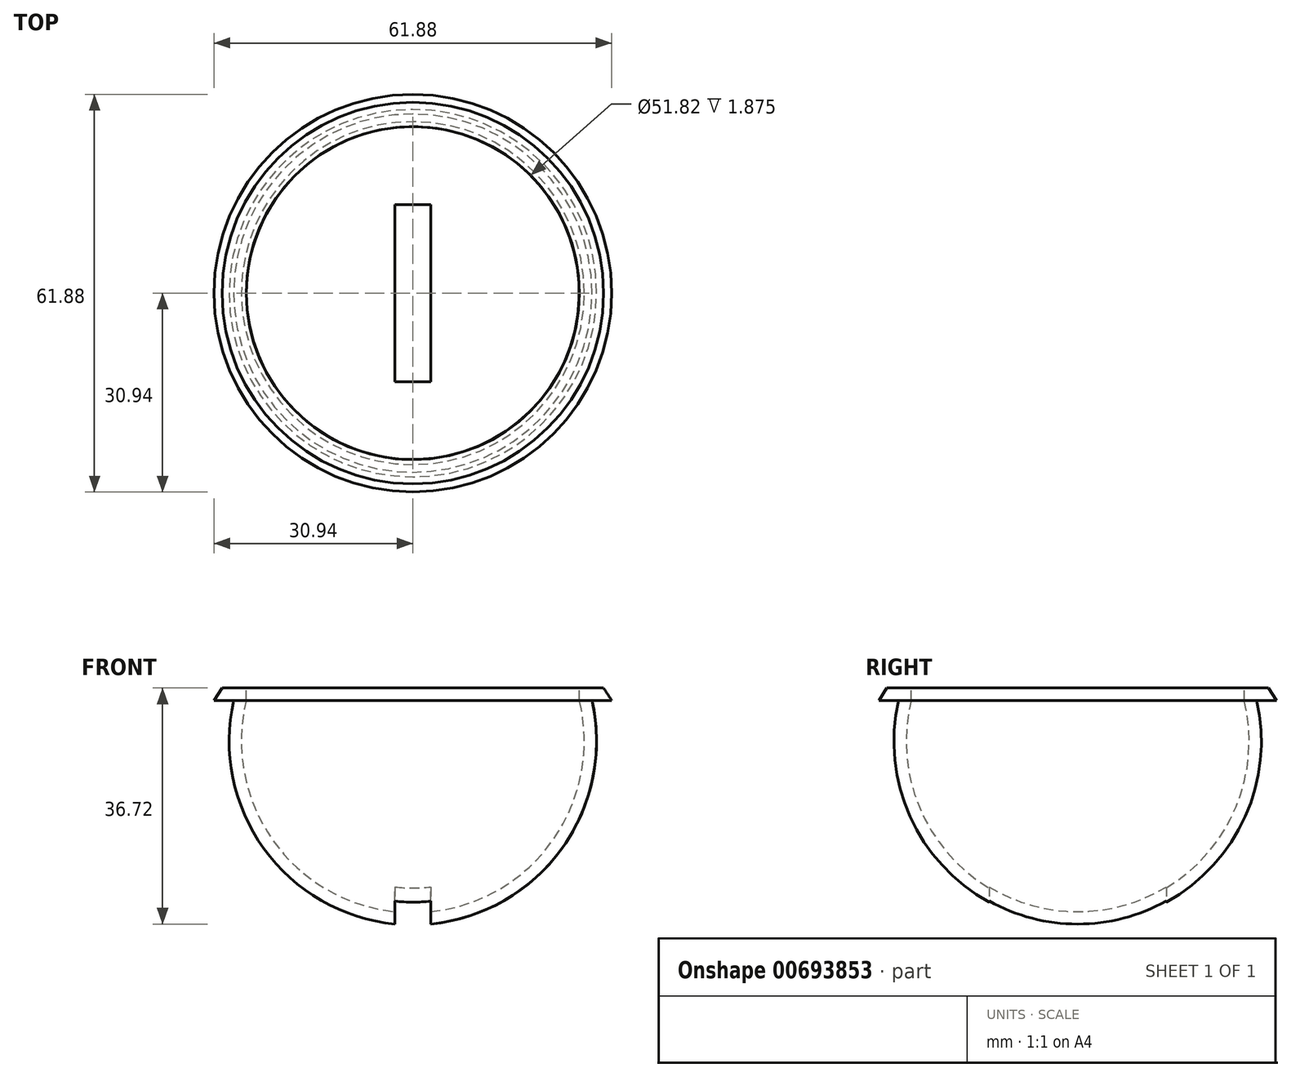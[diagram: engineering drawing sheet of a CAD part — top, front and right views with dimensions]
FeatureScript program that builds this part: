
annotation { "Feature Type Name" : "Feature", "Feature Type Description" : "" }
export const myFeature = defineFeature(function(context is Context, id is Id, definition is map)
    precondition{}
    {
        {
            var Q0;
            Q0=qCreatedBy(makeId("Front.planeOp"),FACE);
            var sketch = newSketch(context, id + "F0", { "sketchPlane" : qUnion([Q0])});
            skCircle(sketch, "E0", {"center": v(0, 0) * mm, "radius": 26.67 * mm});
            skCircle(sketch, "E1", {"center": v(0, 0) * mm, "radius": 28.58 * mm});
            skLineSegment(sketch, "E2", {"start": v(0, 36.4) * mm, "end": v(0, -31.14) * mm});
            skSolve(sketch);
        }
        {
            var Q0;
            {var subQ0=sQuery(id+"F0.wireOp",EDGE,"E2");var subQ1=sQuery(id+"F0.wireOp",EDGE,"E0");var subQ2=makeQuery(id+"F0.imprint","INTERSECT",VERTEX,{"disambiguationData":[OD(0.0)],"derivedFrom":[subQ1,subQ0]});Q0=makeQuery(id+"F0.imprint","IMPRINT",FACE,{"disambiguationData":[TD([[makeQuery(id+"F0.imprint","IMPRINT",EDGE,{"disambiguationData":[TD([[subQ2,-1.0]])],"derivedFrom":subQ1}),-1.0]])]});}
            var Q1;
            Q1=sQuery(id+"F0.wireOp",EDGE,"E2");
            revolve(context, id + "F1", {"entities" : qUnion([Q0]), "axis" : qUnion([Q1]), "revolveType" : RevolveType.FULL});
        }
        {
            var Q0;
            Q0=qCreatedBy(makeId("Front.planeOp"),FACE);
            var sketch = newSketch(context, id + "F2", { "sketchPlane" : qUnion([Q0])});
            skLineSegment(sketch, "E3", {"start": v(0, 23.17) * mm, "end": v(-31.14, 23.17) * mm, "construction": true});
            skLineSegment(sketch, "E4", {"start": v(-31.14, 23.17) * mm, "end": v(32.43, 23.17) * mm, "construction": true});
            skLineSegment(sketch, "E5.bottom", {"start": v(-42, 6.4) * mm, "end": v(42, 6.4) * mm});
            skLineSegment(sketch, "E5.top", {"start": v(-42, 39.93) * mm, "end": v(42, 39.93) * mm});
            skLineSegment(sketch, "E5.left", {"start": v(-42, 6.4) * mm, "end": v(-42, 39.93) * mm});
            skLineSegment(sketch, "E5.right", {"start": v(42, 6.4) * mm, "end": v(42, 39.93) * mm});
            skPoint(sketch, "E5.middle", {"position": v(0, 23.17) * mm});
            skLineSegment(sketch, "E6", {"start": v(0, 39.93) * mm, "end": v(0, 6.4) * mm});
            skSolve(sketch);
        }
        {
            var Q0;
            Q0=qCreatedBy(makeId("Top.planeOp"),FACE);
            cPlane(context, id + "F3", {"entities" : qUnion([Q0]), "cplaneType" : CPlaneType.OFFSET, "offset" : 27.16 * mm, "oppositeDirection" : true, "width" : 152.4 * mm, "height" : 152.4 * mm});
        }
        {
            var Q0;
            Q0=qCreatedBy(id+"F3.planeOp",FACE);
            var sketch = newSketch(context, id + "F4", { "sketchPlane" : qUnion([Q0])});
            skLineSegment(sketch, "E7.bottom", {"start": v(-2.8, -3.18) * mm, "end": v(2.8, -3.18) * mm});
            skLineSegment(sketch, "E7.top", {"start": v(-2.8, 3.18) * mm, "end": v(2.8, 3.18) * mm});
            skLineSegment(sketch, "E7.left", {"start": v(-2.8, -3.18) * mm, "end": v(-2.8, 3.18) * mm});
            skLineSegment(sketch, "E7.right", {"start": v(2.8, -3.18) * mm, "end": v(2.8, 3.18) * mm});
            skPoint(sketch, "E7.middle", {"position": v(0, 0) * mm});
            skCircle(sketch, "E8", {"center": v(0, 0) * mm, "radius": 1.05 * mm});
            skLineSegment(sketch, "E9.bottom", {"start": v(-2.8, -13.78) * mm, "end": v(2.8, -13.78) * mm});
            skLineSegment(sketch, "E9.top", {"start": v(-2.8, 13.78) * mm, "end": v(2.8, 13.78) * mm});
            skLineSegment(sketch, "E9.left", {"start": v(-2.8, -13.78) * mm, "end": v(-2.8, 13.78) * mm});
            skLineSegment(sketch, "E9.right", {"start": v(2.8, -13.78) * mm, "end": v(2.8, 13.78) * mm});
            skSolve(sketch);
        }
        {
            var Q0;
            {var subQ0=sQuery(id+"F0.wireOp",EDGE,"E2");var subQ1=sQuery(id+"F0.wireOp",EDGE,"E0");var subQ2=makeQuery(id+"F0.imprint","INTERSECT",VERTEX,{"disambiguationData":[OD(0.0)],"derivedFrom":[subQ1,subQ0]});Q0=makeQuery(id+"F0.imprint","IMPRINT",FACE,{"disambiguationData":[TD([[makeQuery(id+"F0.imprint","IMPRINT",EDGE,{"disambiguationData":[TD([[subQ2,-1.0]])],"derivedFrom":subQ1}),-1.0]])]});}
            var Q1;
            Q1=sQuery(id+"F0.wireOp",EDGE,"E2");
            revolve(context, id + "F5", {"entities" : qUnion([Q0]), "axis" : qUnion([Q1]), "revolveType" : RevolveType.FULL});
        }
        {
            var Q0;
            Q0=makeQuery(id+"F2.imprint","IMPRINT",FACE,{"disambiguationData":[TD([[makeQuery(id+"F2.imprint","IMPRINT",EDGE,{"derivedFrom":sQuery(id+"F2.wireOp",EDGE,"E5.bottom")}),1.0]])]});
            extrude(context, id + "F6", {"entities" : qUnion([Q0]), "operationType" : NewBodyOperationType.REMOVE, "endBound" : BoundingType.SYMMETRIC, "oppositeDirection" : true, "depth" : 69.6 * mm, "offsetDistance" : 25.4 * mm});
        }
        {
            var Q0;
            {var subQ0=sQuery(id+"F4.wireOp",EDGE,"E7.bottom");Q0=makeQuery(id+"F4.imprint","IMPRINT",FACE,{"disambiguationData":[TD([[makeQuery(id+"F4.imprint","IMPRINT",EDGE,{"derivedFrom":subQ0}),-1.0]])]});}
            var Q1;
            {var subQ0=sQuery(id+"F4.wireOp",EDGE,"E7.top");Q1=makeQuery(id+"F4.imprint","IMPRINT",FACE,{"disambiguationData":[TD([[makeQuery(id+"F4.imprint","IMPRINT",EDGE,{"derivedFrom":subQ0}),1.0]])]});}
            var Q2;
            {var subQ1=sQuery(id+"F4.wireOp",EDGE,"E7.bottom");Q2=makeQuery(id+"F4.imprint","IMPRINT",FACE,{"disambiguationData":[TD([[makeQuery(id+"F4.imprint","IMPRINT",EDGE,{"derivedFrom":subQ1}),1.0]])]});}
            var Q3;
            Q3=makeQuery(id+"F4.imprint","IMPRINT",FACE,{"disambiguationData":[TD([[makeQuery(id+"F4.imprint","IMPRINT",EDGE,{"derivedFrom":sQuery(id+"F4.wireOp",EDGE,"E8")}),1.0]])]});
            extrude(context, id + "F7", {"entities" : qUnion([Q0, Q1, Q2, Q3]), "operationType" : NewBodyOperationType.REMOVE, "depth" : 25.4 * mm, "offsetDistance" : 25.4 * mm});
        }
        {
            var Q0;
            {var subQ0=sQuery(id+"F4.wireOp",EDGE,"E7.bottom");Q0=makeQuery(id+"F4.imprint","IMPRINT",FACE,{"disambiguationData":[TD([[makeQuery(id+"F4.imprint","IMPRINT",EDGE,{"derivedFrom":subQ0}),-1.0]])]});}
            extrude(context, id + "F8", {"entities" : qUnion([Q0]), "operationType" : NewBodyOperationType.REMOVE, "oppositeDirection" : true, "depth" : 25.4 * mm, "offsetDistance" : 25.4 * mm});
        }
        {
            var Q0;
            {var subQ0=sQuery(id+"F4.wireOp",EDGE,"E7.top");Q0=makeQuery(id+"F4.imprint","IMPRINT",FACE,{"disambiguationData":[TD([[makeQuery(id+"F4.imprint","IMPRINT",EDGE,{"derivedFrom":subQ0}),1.0]])]});}
            extrude(context, id + "F9", {"entities" : qUnion([Q0]), "operationType" : NewBodyOperationType.REMOVE, "oppositeDirection" : true, "depth" : 25.4 * mm, "offsetDistance" : 25.4 * mm});
        }
        {
            var Q0;
            Q0=makeQuery(id+"F4.imprint","IMPRINT",FACE,{"disambiguationData":[TD([[makeQuery(id+"F4.imprint","IMPRINT",EDGE,{"derivedFrom":sQuery(id+"F4.wireOp",EDGE,"E8")}),1.0]])]});
            var Q1;
            {var subQ1=sQuery(id+"F4.wireOp",EDGE,"E7.bottom");Q1=makeQuery(id+"F4.imprint","IMPRINT",FACE,{"disambiguationData":[TD([[makeQuery(id+"F4.imprint","IMPRINT",EDGE,{"derivedFrom":subQ1}),1.0]])]});}
            extrude(context, id + "F10", {"entities" : qUnion([Q0, Q1]), "operationType" : NewBodyOperationType.REMOVE, "endBound" : BoundingType.SYMMETRIC, "depth" : 25.4 * mm, "offsetDistance" : 25.4 * mm});
        }
        {
            var Q0;
            Q0=qCreatedBy(makeId("Front.planeOp"),FACE);
            var sketch = newSketch(context, id + "F11", { "sketchPlane" : qUnion([Q0])});
            skLineSegment(sketch, "E10", {"start": v(-27.85, 6.35) * mm, "end": v(-30.94, 6.35) * mm});
            skLineSegment(sketch, "E11", {"start": v(-30.94, 6.35) * mm, "end": v(-29.67, 8.28) * mm});
            skLineSegment(sketch, "E12", {"start": v(-29.67, 8.28) * mm, "end": v(-25.9, 8.28) * mm});
            skLineSegment(sketch, "E13", {"start": v(-25.9, 8.28) * mm, "end": v(-25.9, 6.35) * mm});
            skLineSegment(sketch, "E14", {"start": v(-25.9, 6.35) * mm, "end": v(-27.85, 6.35) * mm});
            skSolve(sketch);
        }
        {
            var Q0;
            Q0=makeQuery(id+"F11.imprint","IMPRINT",FACE,{"disambiguationData":[TD([[makeQuery(id+"F11.imprint","IMPRINT",EDGE,{"derivedFrom":sQuery(id+"F11.wireOp",EDGE,"E10")}),-1.0]])]});
            var Q1;
            Q1=sQuery(id+"F2.wireOp",EDGE,"E6");
            revolve(context, id + "F12", {"operationType" : NewBodyOperationType.ADD, "entities" : qUnion([Q0]), "axis" : qUnion([Q1]), "revolveType" : RevolveType.FULL});
        }
    });
